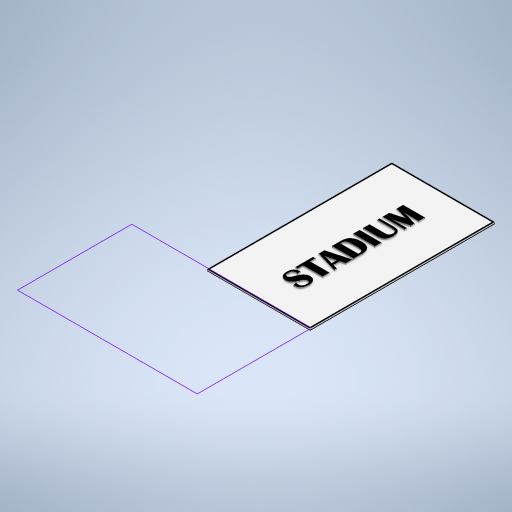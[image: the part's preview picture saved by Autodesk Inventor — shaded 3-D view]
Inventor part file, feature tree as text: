
AUTODESK INVENTOR PART (.ipt)
format: ipt  version: 2024.1 (Build 281209000, 209)  size: 378,880 bytes
history: native  units: in
note: dims shown in document units (in); Inventor stores cm internally (conversion verified against a paired STEP export)
features: extrude x3, sketch x2
ambient origin geometry x8: Origin, YZ Plane, XZ Plane, XY Plane, X Axis, Y Axis, Z Axis, Center Point
bodies: Solid1 (feature_tree), Solid2 (feature_tree), Solid3 (feature_tree)
feature tree (5):
  sketch  "Sketch1"  dims[d3=20.0in d4=0.0in d5=10.0in d6=0.0in]
  extrude  "Extrusion1"  Depth=10.0in TaperAngle=0.0deg
  extrude  "Extrusion2"  Depth=0.5in
  extrude  "Extrusion3"  Depth=0.0344in
  sketch  "Sketch2"  dims[d7=10.0in d8=0.0in d9=0.5in d10=0.0344in d11=0.5in d12=0.0344in]
